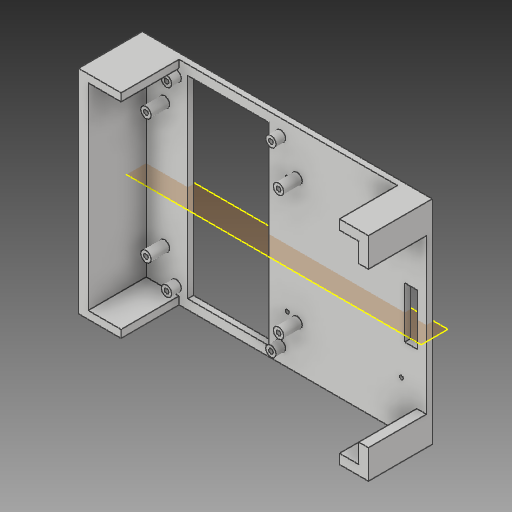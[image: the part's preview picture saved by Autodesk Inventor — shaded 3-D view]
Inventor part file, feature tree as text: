
AUTODESK INVENTOR PART (.ipt)
format: ipt  version: 2019 (Build 230136000, 136)  size: 242,176 bytes
history: native  units: mm
features: sketch x7, reference x6, extrude x4, other x4, plane x3, hole x3, mirror x1, projected_geometry x1
ambient origin geometry x8: Origin, YZ Plane, XZ Plane, XY Plane, X Axis, Y Axis, Z Axis, Center Point
bodies: Solid1 (feature_tree)
feature tree (29):
  extrude  "Extrusion1"  Depth=150.0mm
  sketch  "Sketch2"  dims[d2=8.0mm d3=1.0mm]
  plane  "Work Plane1"
  extrude  "Extrusion2"  Depth=1.0mm
  hole  "Hole1"  [1 undecoded]
  hole  "Hole2"  [1 undecoded]
  sketch  "Sketch5"  dims[d10=2.459mm d11=4.0mm d12=6.3mm d13=2.0mm d14=90.0deg d15=5.0mm d16=20.594885mm]
  plane  "Work Plane2"
  extrude  "Extrusion3"  Depth=1.0mm
  hole  "Hole3"  [1 undecoded]
  plane  "Work Plane3"
  mirror  "Mirror1"
  extrude  "Extrusion4"  Depth=22.0mm
  sketch  "Sketch1"  dims[d0=110.0mm d1=150.0mm]
  reference  "Reference1"
  reference  "Reference2"
  reference  "Reference3"
  sketch  "Sketch3"  dims[d4=0.75mm d5=3.0mm d6=0.0mm]
  reference  "Reference4"
  sketch  "Sketch4"  dims[d7=1.0mm d8=3.0mm d9=0.0mm]
  reference  "Reference5"
  reference  "Reference6"
  sketch  "Sketch6"  dims[d17=2.013mm d18=5.0mm d19=6.3mm d20=2.0mm d21=90.0deg d22=7.6mm d23=20.594885mm d24=1.0mm]
  sketch  "Sketch7"  dims[d25=3.0mm d26=0.0mm d27=2.459mm d28=6.0mm d29=6.3mm d30=2.0mm d31=90.0deg d32=8.8mm d33=20.594885mm d34=5.0mm d35=22.0mm d36=4.0mm d37=15.0mm d38=5.0mm d39=30.0mm d40=0.0mm]
  projected_geometry  "Projected Loop1"
  other  "Assembly1"
  other  "LCD Screen:1"
  other  "Keypad:1"
  other  "PCB:1"
note: 3 required parameter values undecoded (feature->parameter linkage not recoverable at this tier; creation-order binding heuristic only, values carry confidence <= 0.55)
